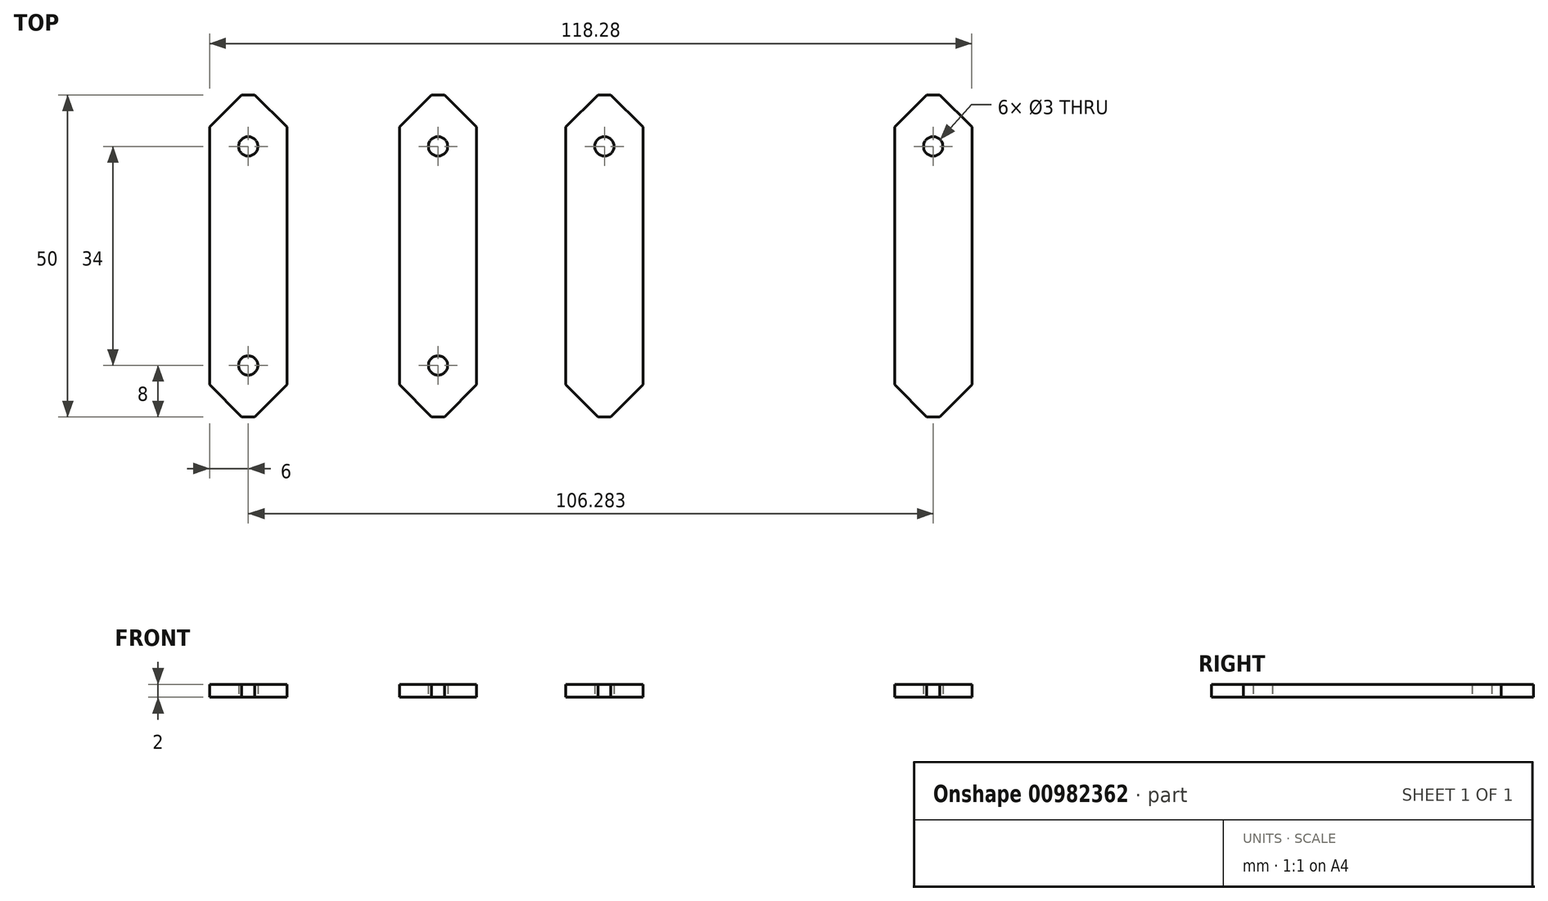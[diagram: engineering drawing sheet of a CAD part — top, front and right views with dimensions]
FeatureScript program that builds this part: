
annotation { "Feature Type Name" : "Feature", "Feature Type Description" : "" }
export const myFeature = defineFeature(function(context is Context, id is Id, definition is map)
    precondition{}
    {
        {
            var Q0;
            Q0=qCreatedBy(makeId("Top.planeOp"),FACE);
            var sketch = newSketch(context, id + "F0", { "sketchPlane" : qUnion([Q0])});
            skLineSegment(sketch, "E0.bottom", {"start": v(0, 0) * mm, "end": v(12, 0) * mm});
            skLineSegment(sketch, "E0.top", {"start": v(0, 50) * mm, "end": v(12, 50) * mm});
            skLineSegment(sketch, "E0.left", {"start": v(0, 0) * mm, "end": v(0, 50) * mm});
            skLineSegment(sketch, "E0.right", {"start": v(12, 0) * mm, "end": v(12, 50) * mm});
            skLineSegment(sketch, "E1", {"start": v(20.72, 51.05) * mm, "end": v(20.72, 0) * mm, "construction": true});
            skLineSegment(sketch, "E2", {"start": v(48.36, 52.74) * mm, "end": v(48.36, -3.2) * mm, "construction": true});
            skLineSegment(sketch, "E3", {"start": v(86.77, 55.77) * mm, "end": v(86.77, -4.21) * mm, "construction": true});
            skLineSegment(sketch, "E4", {"start": v(116.1, 47.35) * mm, "end": v(116.1, -21.4) * mm, "construction": true});
            skLineSegment(sketch, "E5.MirrorCS", {"start": v(-6.9, 52.74) * mm, "end": v(-6.9, -3.2) * mm, "construction": true});
            skLineSegment(sketch, "E6.MirrorCS", {"start": v(41.45, 0) * mm, "end": v(41.45, 50) * mm});
            skLineSegment(sketch, "E7.MirrorCS", {"start": v(29.45, 0) * mm, "end": v(29.45, 50) * mm});
            skLineSegment(sketch, "E8.MirrorCS", {"start": v(41.45, 50) * mm, "end": v(29.45, 50) * mm});
            skLineSegment(sketch, "E9.MirrorCS", {"start": v(41.45, 0) * mm, "end": v(29.45, 0) * mm});
            skLineSegment(sketch, "E10.MirrorCS", {"start": v(55.27, 0) * mm, "end": v(67.27, 0) * mm});
            skLineSegment(sketch, "E11.MirrorCS", {"start": v(55.27, 50) * mm, "end": v(67.27, 50) * mm});
            skLineSegment(sketch, "E12.MirrorCS", {"start": v(67.27, 0) * mm, "end": v(67.27, 50) * mm});
            skLineSegment(sketch, "E13.MirrorCS", {"start": v(55.27, 0) * mm, "end": v(55.27, 50) * mm});
            skLineSegment(sketch, "E14.MirrorCS", {"start": v(106.28, 0) * mm, "end": v(106.28, 50) * mm});
            skLineSegment(sketch, "E15.MirrorCS", {"start": v(118.28, 0) * mm, "end": v(118.28, 50) * mm});
            skLineSegment(sketch, "E16.MirrorCS", {"start": v(118.28, 50) * mm, "end": v(106.28, 50) * mm});
            skLineSegment(sketch, "E17.MirrorCS", {"start": v(118.28, 0) * mm, "end": v(106.28, 0) * mm});
            skLineSegment(sketch, "E18", {"start": v(35.45, 50) * mm, "end": v(35.45, 42) * mm, "construction": true});
            skCircle(sketch, "E19", {"center": v(35.45, 42) * mm, "radius": 1.5 * mm});
            skCircle(sketch, "E20.MirrorC", {"center": v(6, 42) * mm, "radius": 1.5 * mm});
            skCircle(sketch, "E21.MirrorC", {"center": v(61.27, 42) * mm, "radius": 1.5 * mm});
            skCircle(sketch, "E22.MirrorC", {"center": v(112.28, 42) * mm, "radius": 1.5 * mm});
            skLineSegment(sketch, "E23", {"start": v(6, 0) * mm, "end": v(6, 8) * mm, "construction": true});
            skCircle(sketch, "E24", {"center": v(6, 8) * mm, "radius": 1.5 * mm});
            skCircle(sketch, "E25.MirrorC", {"center": v(35.45, 8) * mm, "radius": 1.5 * mm});
            skSolve(sketch);
        }
        {
            var Q0;
            Q0=makeQuery(id+"F0.imprint","IMPRINT",FACE,{"disambiguationData":[TD([[makeQuery(id+"F0.imprint","IMPRINT",EDGE,{"derivedFrom":sQuery(id+"F0.wireOp",EDGE,"E6.MirrorCS")}),1.0]])]});
            var Q1;
            Q1=makeQuery(id+"F0.imprint","IMPRINT",FACE,{"disambiguationData":[TD([[makeQuery(id+"F0.imprint","IMPRINT",EDGE,{"derivedFrom":sQuery(id+"F0.wireOp",EDGE,"E10.MirrorCS")}),1.0]])]});
            var Q2;
            Q2=makeQuery(id+"F0.imprint","IMPRINT",FACE,{"disambiguationData":[TD([[makeQuery(id+"F0.imprint","IMPRINT",EDGE,{"derivedFrom":sQuery(id+"F0.wireOp",EDGE,"E14.MirrorCS")}),-1.0]])]});
            var Q3;
            Q3=makeQuery(id+"F0.imprint","IMPRINT",FACE,{"disambiguationData":[TD([[makeQuery(id+"F0.imprint","IMPRINT",EDGE,{"derivedFrom":sQuery(id+"F0.wireOp",EDGE,"E0.bottom")}),1.0]])]});
            extrude(context, id + "F1", {"entities" : qUnion([Q0, Q1, Q2, Q3]), "depth" : 2 * mm, "offsetDistance" : 25 * mm});
        }
        {
            var Q0;
            Q0=makeQuery(id+"F1.opExtrude","SWEPT_EDGE",EDGE,{"disambiguationData":[OSD([sQuery(id+"F0.wireOp",EDGE,"E15.MirrorCS"),sQuery(id+"F0.wireOp",EDGE,"E17.MirrorCS")])]});
            var Q1;
            Q1=makeQuery(id+"F1.opExtrude","SWEPT_EDGE",EDGE,{"disambiguationData":[OSD([sQuery(id+"F0.wireOp",EDGE,"E10.MirrorCS"),sQuery(id+"F0.wireOp",EDGE,"E12.MirrorCS")])]});
            var Q2;
            Q2=makeQuery(id+"F1.opExtrude","SWEPT_EDGE",EDGE,{"disambiguationData":[OSD([sQuery(id+"F0.wireOp",EDGE,"E6.MirrorCS"),sQuery(id+"F0.wireOp",EDGE,"E9.MirrorCS")])]});
            var Q3;
            Q3=makeQuery(id+"F1.opExtrude","SWEPT_EDGE",EDGE,{"disambiguationData":[OSD([sQuery(id+"F0.wireOp",EDGE,"E0.bottom"),sQuery(id+"F0.wireOp",EDGE,"E0.right")])]});
            var Q4;
            Q4=makeQuery(id+"F1.opExtrude","SWEPT_EDGE",EDGE,{"disambiguationData":[OSD([sQuery(id+"F0.wireOp",EDGE,"E0.bottom"),sQuery(id+"F0.wireOp",EDGE,"E0.left")])]});
            var Q5;
            Q5=makeQuery(id+"F1.opExtrude","SWEPT_EDGE",EDGE,{"disambiguationData":[OSD([sQuery(id+"F0.wireOp",EDGE,"E7.MirrorCS"),sQuery(id+"F0.wireOp",EDGE,"E9.MirrorCS")])]});
            var Q6;
            Q6=makeQuery(id+"F1.opExtrude","SWEPT_EDGE",EDGE,{"disambiguationData":[OSD([sQuery(id+"F0.wireOp",EDGE,"E10.MirrorCS"),sQuery(id+"F0.wireOp",EDGE,"E13.MirrorCS")])]});
            var Q7;
            Q7=makeQuery(id+"F1.opExtrude","SWEPT_EDGE",EDGE,{"disambiguationData":[OSD([sQuery(id+"F0.wireOp",EDGE,"E14.MirrorCS"),sQuery(id+"F0.wireOp",EDGE,"E17.MirrorCS")])]});
            var Q8;
            Q8=makeQuery(id+"F1.opExtrude","SWEPT_EDGE",EDGE,{"disambiguationData":[OSD([sQuery(id+"F0.wireOp",EDGE,"E15.MirrorCS"),sQuery(id+"F0.wireOp",EDGE,"E16.MirrorCS")])]});
            var Q9;
            Q9=makeQuery(id+"F1.opExtrude","SWEPT_EDGE",EDGE,{"disambiguationData":[OSD([sQuery(id+"F0.wireOp",EDGE,"E11.MirrorCS"),sQuery(id+"F0.wireOp",EDGE,"E12.MirrorCS")])]});
            var Q10;
            Q10=makeQuery(id+"F1.opExtrude","SWEPT_EDGE",EDGE,{"disambiguationData":[OSD([sQuery(id+"F0.wireOp",EDGE,"E6.MirrorCS"),sQuery(id+"F0.wireOp",EDGE,"E8.MirrorCS")])]});
            var Q11;
            Q11=makeQuery(id+"F1.opExtrude","SWEPT_EDGE",EDGE,{"disambiguationData":[OSD([sQuery(id+"F0.wireOp",EDGE,"E0.top"),sQuery(id+"F0.wireOp",EDGE,"E0.right")])]});
            var Q12;
            Q12=makeQuery(id+"F1.opExtrude","SWEPT_EDGE",EDGE,{"disambiguationData":[OSD([sQuery(id+"F0.wireOp",EDGE,"E14.MirrorCS"),sQuery(id+"F0.wireOp",EDGE,"E16.MirrorCS")])]});
            var Q13;
            Q13=makeQuery(id+"F1.opExtrude","SWEPT_EDGE",EDGE,{"disambiguationData":[OSD([sQuery(id+"F0.wireOp",EDGE,"E11.MirrorCS"),sQuery(id+"F0.wireOp",EDGE,"E13.MirrorCS")])]});
            var Q14;
            Q14=makeQuery(id+"F1.opExtrude","SWEPT_EDGE",EDGE,{"disambiguationData":[OSD([sQuery(id+"F0.wireOp",EDGE,"E7.MirrorCS"),sQuery(id+"F0.wireOp",EDGE,"E8.MirrorCS")])]});
            var Q15;
            Q15=makeQuery(id+"F1.opExtrude","SWEPT_EDGE",EDGE,{"disambiguationData":[OSD([sQuery(id+"F0.wireOp",EDGE,"E0.top"),sQuery(id+"F0.wireOp",EDGE,"E0.left")])]});
            chamfer(context, id + "F2", {"entities" : qUnion([Q0, Q1, Q2, Q3, Q4, Q5, Q6, Q7, Q8, Q9, Q10, Q11, Q12, Q13, Q14, Q15]), "width" : 5 * mm, "tangentPropagation" : true});
        }
    });
